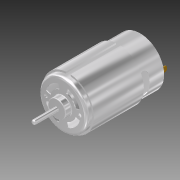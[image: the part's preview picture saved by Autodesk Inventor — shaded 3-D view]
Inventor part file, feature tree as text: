
AUTODESK INVENTOR PART (.ipt)
format: ipt  version: 2012 (Build 160160000, 160)  size: 300,032 bytes
history: native  units: mm (DEFAULTED — no unit token found)
features: sketch x15, extrude x13, fillet x3, plane x3, hole x2, mirror x2, pattern_circular x2, shell x1, chamfer x1
ambient origin geometry x8: Origin, YZ Plane, XZ Plane, XY Plane, X Axis, Y Axis, Z Axis, Center Point
bodies: Solid1 (feature_tree)
feature tree (42):
  extrude  "Extrusion1"  Depth=57.25mm TaperAngle=0.0deg
  fillet  "Fillet1"  Radius=2.0mm
  shell  "Shell1"  Thickness=0.62mm
  extrude  "Extrusion2"  Depth=4.5mm TaperAngle=0.0deg
  fillet  "Fillet2"  Radius=0.5mm
  extrude  "Extrusion3"  Depth=18.0mm TaperAngle=0.0deg
  fillet  "Fillet3"  Radius=1.6mm
  hole  "Hole1"  [1 undecoded]
  mirror  "Mirror1"
  extrude  "Extrusion4"  Depth=13.0mm
  pattern_circular  "Circular Pattern1"  Count=4 Angle=360.0deg
  plane  "Work Plane1"
  extrude  "Extrusion5"  Depth=0.62mm TaperAngle=0.0deg
  extrude  "Extrusion6"  Depth=0.62mm TaperAngle=0.0deg
  extrude  "Extrusion7"  Depth=3.0mm TaperAngle=0.0deg
  extrude  "Extrusion8"  Depth=0.8mm TaperAngle=0.0deg
  extrude  "Extrusion9"  Depth=1.0mm TaperAngle=0.0deg
  extrude  "Extrusion10"  Depth=3.15mm
  pattern_circular  "Circular Pattern2"  [2 undecoded]
  extrude  "Extrusion11"  Depth=1.0mm TaperAngle=0.0deg
  chamfer  "Chamfer1"  Distance=40.0mm Angle=360.0deg
  hole  "Hole2"  [1 undecoded]
  mirror  "Mirror2"
  plane  "Work Plane2"
  extrude  "Extrusion12"  Depth=3.8mm
  plane  "Work Plane3"
  extrude  "Extrusion13"  Depth=14.0mm
  sketch  "Sketch1"  dims[d0=35.5mm d1=57.25mm d2=0.0mm d3=2.0mm d4=0.62mm]
  sketch  "Sketch2"  dims[d5=13.0mm d6=4.5mm d7=0.0mm d8=0.5mm]
  sketch  "Sketch3"  dims[d9=3.2mm d10=18.0mm d11=0.0mm d12=1.6mm]
  sketch  "Sketch4"  dims[d13=12.5mm]
  sketch  "Sketch5"  dims[d14=2.5mm d15=6.0mm d16=4.0mm d17=2.0mm d18=14.3117mm d19=8.0mm d20=20.594885mm d21=15.0deg]
  sketch  "Sketch6"  dims[d22=15.0deg d23=13.0mm]
  sketch  "Sketch7"  dims[d24=9.5mm]
  sketch  "Sketch8"  dims[d25=10.0mm d26=0.0mm d27=40.0mm d29=360.0deg]
  sketch  "Sketch9"  dims[d30=-1.75mm d31=0.62mm d32=0.0mm]
  sketch  "Sketch10"  dims[d33=24.0mm d34=0.62mm d35=0.0mm]
  sketch  "Sketch11"  dims[d36=10.75mm d37=3.0mm d38=0.0mm]
  sketch  "Sketch12"  dims[d39=6.9mm d40=0.8mm d41=0.0mm]
  sketch  "Sketch13"  dims[d42=3.2mm d43=1.0mm d44=0.0mm]
  sketch  "Sketch14"  dims[d45=3.15mm d46=3.15mm]
  sketch  "Sketch15"  dims[d47=9.875mm d48=6.5mm d49=1.0mm d50=0.0mm d51=40.0mm d53=360.0deg d54=0.5mm d55=3.8mm d56=14.0mm d57=7.2mm d58=0.0mm d59=1.0mm d60=2.0mm d61=3.0mm d62=2.0mm d63=6.0mm d64=4.0mm d65=2.0mm d66=14.3117mm d67=1.0mm d68=20.594885mm d69=18.0mm d70=10.75mm d71=5.9mm d72=9.85mm d73=7.2mm d74=0.0mm d75=-4.0mm d76=38.0mm d77=3.5mm d78=37.0mm d79=0.0mm d80=45.0deg]
note: 4 required parameter values undecoded (feature->parameter linkage not recoverable at this tier; creation-order binding heuristic only, values carry confidence <= 0.55)
